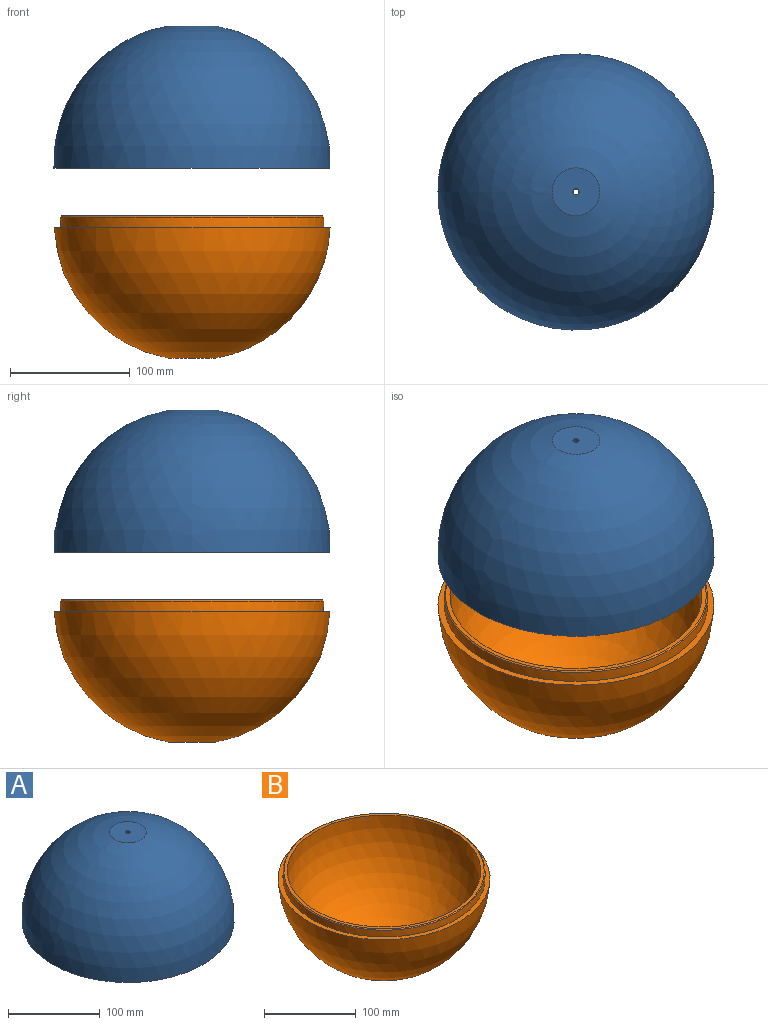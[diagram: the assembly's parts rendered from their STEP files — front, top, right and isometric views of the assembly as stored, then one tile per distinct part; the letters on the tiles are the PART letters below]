
ASSEMBLY  parts=2 mates=1
PART A: 8 faces, bbox 231x231x118.8 mm
  f0: sphere r=105.5mm, area 66598.6mm2, adj f2,f6
  f1: cylinder r=111mm len=222mm, axis (0,0,-1), area 6276.9mm2, adj f2,f7
  f2: plane 222x222mm, normal (0,0,-1), area 3819.4mm2, adj f0,f1
  f3: plane 40x40mm, normal (0,0,1), area 1236.2mm2, adj f4,f6
  f4: sphere r=115.5mm, area 86181.6mm2, adj f3,f5
  f5: plane 230.78x230.78mm, normal (0,0,-1), area 2423mm2, adj f4,f7
  f6: cylinder r=2.55mm len=8.29mm, axis (0,0,1), area 132.9mm2, adj f0,f3
  f7: cone r=111mm half-angle=45deg, axis (0,0,-1), area 990.8mm2, adj f1,f5
PART B: 8 faces, bbox 230.8x230.8x118.8 mm
  f0: sphere r=105.5mm, area 73227.3mm2, adj f1,f7
  f1: plane 218x218mm, normal (0,0,1), area 2437.1mm2, adj f0,f6
  f2: cylinder r=110mm len=220mm, axis (0,0,1), area 6220.4mm2, adj f3,f6
  f3: plane 230.78x230.78mm, normal (0,0,1), area 3817.8mm2, adj f2,f4
  f4: sphere r=115.5mm, area 78924.5mm2, adj f3,f5
  f5: plane 40x40mm, normal (0,0,-1), area 1236.2mm2, adj f4,f7
  f6: cone r=109mm half-angle=45deg, axis (0,0,-1), area 973mm2, adj f1,f2
  f7: cylinder r=2.55mm len=8.29mm, axis (0,0,-1), area 132.9mm2, adj f0,f5
PLACE A at identity
PLACE B t=(0,0,-50)mm
MATE revolute B.f7 <-> A.f1  axis (0,0,1) through (0,0,-50)mm
